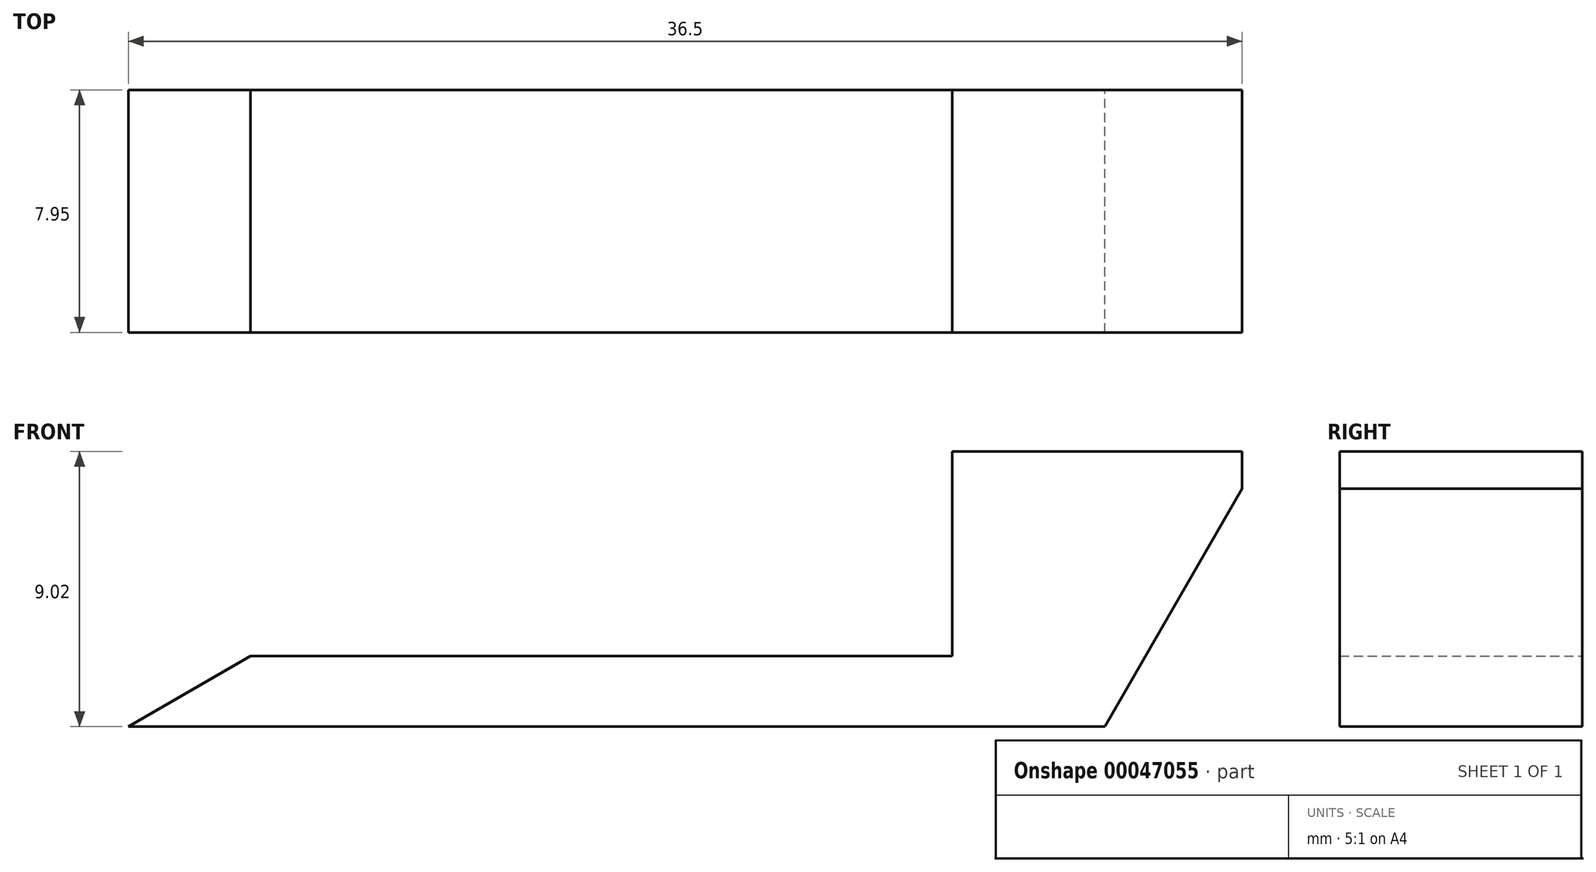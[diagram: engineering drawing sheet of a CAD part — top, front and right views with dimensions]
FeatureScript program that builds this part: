
annotation { "Feature Type Name" : "Feature", "Feature Type Description" : "" }
export const myFeature = defineFeature(function(context is Context, id is Id, definition is map)
    precondition{}
    {
        {
            var Q0;
            Q0=qCreatedBy(makeId("Front.planeOp"),FACE);
            var sketch = newSketch(context, id + "F0", { "sketchPlane" : qUnion([Q0])});
            skLineSegment(sketch, "E0", {"start": v(0, 0) * mm, "end": v(4.1, 4.1) * mm});
            skLineSegment(sketch, "E1", {"start": v(27, 9.02) * mm, "end": v(27, 9.02) * mm});
            skLineSegment(sketch, "E2", {"start": v(27, 9.02) * mm, "end": v(36.5, 9.02) * mm});
            skLineSegment(sketch, "E3", {"start": v(36.5, 9.02) * mm, "end": v(36.5, 0) * mm});
            skLineSegment(sketch, "E4", {"start": v(36.5, 0) * mm, "end": v(0, 0) * mm});
            skLineSegment(sketch, "E5", {"start": v(0, 0) * mm, "end": v(0, -0.2) * mm, "construction": true});
            skLineSegment(sketch, "E6", {"start": v(0, -0.2) * mm, "end": v(3, -0.2) * mm, "construction": true});
            skLineSegment(sketch, "E7", {"start": v(3, -0.2) * mm, "end": v(3, 0) * mm, "construction": true});
            skLineSegment(sketch, "E8", {"start": v(3, 0) * mm, "end": v(10.45, 7.45) * mm, "construction": true});
            skLineSegment(sketch, "E9", {"start": v(0, 0) * mm, "end": v(15.84, 9.14) * mm});
            skLineSegment(sketch, "E10", {"start": v(27, 4.1) * mm, "end": v(4.1, 4.1) * mm});
            skPoint(sketch, "E11", {"position": v(7.1, 4.1) * mm});
            skLineSegment(sketch, "E12", {"start": v(27, 9.02) * mm, "end": v(27, 4.1) * mm});
            skLineSegment(sketch, "E13", {"start": v(4, 2.3) * mm, "end": v(27, 2.3) * mm});
            skLineSegment(sketch, "E14", {"start": v(27, 2.3) * mm, "end": v(27, 4.1) * mm});
            skLineSegment(sketch, "E15", {"start": v(27, 0) * mm, "end": v(27, -0.2) * mm, "construction": true});
            skLineSegment(sketch, "E16", {"start": v(27, -0.2) * mm, "end": v(32, -0.2) * mm, "construction": true});
            skLineSegment(sketch, "E17", {"start": v(32, -0.2) * mm, "end": v(32, 0) * mm, "construction": true});
            skLineSegment(sketch, "E18", {"start": v(32, 0) * mm, "end": v(36.5, 7.8) * mm});
            skLineSegment(sketch, "E19", {"start": v(25.41, 0) * mm, "end": v(32, 0) * mm});
            skLineSegment(sketch, "E20", {"start": v(32, 0) * mm, "end": v(29.65, 8.75) * mm, "construction": true});
            skLineSegment(sketch, "E21", {"start": v(27, 2.3) * mm, "end": v(34.7, 10) * mm, "construction": true});
            skLineSegment(sketch, "E22", {"start": v(24.8, 1.23) * mm, "end": v(32.67, 1.16) * mm, "construction": true});
            skLineSegment(sketch, "E23", {"start": v(32.67, 1.16) * mm, "end": v(28.3, 10.09) * mm, "construction": true});
            skArc(sketch, "E24", {"start": v(36.5, 5.7) * mm, "mid": v(33.86, 3.16) * mm, "end": v(32, 0) * mm, "construction": true});
            skSolve(sketch);
        }
        {
            var Q0;
            {var subQ4=sQuery(id+"F0.wireOp",EDGE,"E2");Q0=makeQuery(id+"F0.imprint","IMPRINT",FACE,{"disambiguationData":[TD([[makeQuery(id+"F0.imprint","IMPRINT",EDGE,{"derivedFrom":subQ4}),-1.0]])]});}
            extrude(context, id + "F1", {"entities" : qUnion([Q0]), "depth" : 7.95 * mm});
        }
    });
